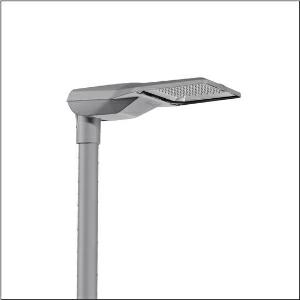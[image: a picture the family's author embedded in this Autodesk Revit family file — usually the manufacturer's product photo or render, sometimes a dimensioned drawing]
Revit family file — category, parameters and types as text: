
# Revit family: streetlight_sl_21_iq_midi___st0_5a_5xe3b31g08mb_2812
name_source: partatom
category: Lighting Fixtures
units: mm (PartAtom-declared; Revit-internal decimal feet)

## family parameters
Cut with Voids When Loaded = No
Host = Face
Light Source = No
Part Type = Normal
Room Calculation Point = No
Round Connector Dimension = Use Diameter
Shared = No

## types (1)
- --- (1 x LED, 19500 lm, 146.7 W, 3000K)
    Apparent Load = 147 VA
    CIE Flux Codes = 41 75 97 100 100
    Color Rendering = 70
    Color Temperature = 3000K
    Default Elevation = 1800 mm
    Description = Streetlight SL 21 iQ midi, mast luminaire, primary light control with lens, of PMMA, primary optical cover: cover, of toughened safety glass, transparent, light distribution: ST0.5a, light emission: direct distribution, primary light characteristic: asymmetric, installation type: post-top, side-entry, LED, High Power LED, rated luminous flux: 19.500lm, luminous efficacy: 133lm/W, light colour: 730, colour temperature: 3000K, control: Street-Remote, Auto-Match, Temp-Guard, Lumen-Switch, Night-Set, Smart-Wire, Light-Fading, Desk-Remote (wireless, voltage-free reading and setting of iQ features in the workshop via application-optimized NFC function/RFID function), optimised constant luminous flux control (CLO 2.0), presetting dimming linear, mains connection: 230..240V, AC, 50/60Hz, start of lifetime: 147W, end of service life: 161W, reduction: 62W, luminaire housing, of diecast aluminium, powder-coated, Siteco® metallic grey (DB 702S), corrosivity category C5 mid according to DIN EN ISO 12944, please order mast flange separately, inclination adjustable: 0°, 5°, 10°, 15°, sealing non-destructively replaceable, multi-level sealing system, length: 644mm, width: 335mm, height: 110mm, mast flange for spigot size: 42mm (side-entry): 5XC10008XM4, 60/48mm (side-entry/post-top): 5XC10108XM2, 76/60mm (side-entry/post-top): 5XC10108XM1, protection rating (complete): IP66, insulation class (complete): insulation class II (safety insulation), certification: CE, ENEC, ENEC+, VDE, impact resistance: IK09, permissible operating ambient temperature for outdoor applications: -40..+50°C, standard-compliant lighting for roads and squares, packaging unit: 1 piece

Light Distribution: ST0.5a
    Height = 111 mm
    Lamp = 1 x LED
    Lamp Light Flux = 19500 lm
    Lamp Power = 146.7 W
    Lamp count = 1
    Length = 644 mm
    Luminous efficacy = 133 lm/W
    Manufacturer = Siteco
    ModVariant = No
    Model = 5XE3B31G08MB
    Number of Poles = 1
    OnlyDefault = Yes
    Power Factor = 1
    Product Name = Streetlight SL 21 iQ midi | ST0.5a
    Product group = mast luminaire | pylon top
    ProductGroupID = 6100
    Protection Class = Protection class II
    Protection Degree = IP 66
    RLX_Detail_Level = 1
    RLX_Emergency_Light_Flux = 0 lm
    RLX_Emergency_Type = 0
    RLX_Emergency_Type_DB = No
    RlxData = <blob elided: 101705 chars, md5=e67770d6>
    Socket = socket
    Standby Power = 0 W
    System Light Flux = 19499 lm
    System Power = 147 W
    Type Comments = factory setting: luminous flux: 100 % | dim-lin: 254 | 753 mA
    Type Image = l_1004298.jpg
    URL = http://relux.com
    VarID = @adj_144463
    Voltage = 0 V
    Weight = 0.00 kg
    Width = 336 mm

## geometry (parser evidence)
native form markers: Blend x4, Sweep x10
no freeform markers — native parametric forms only
